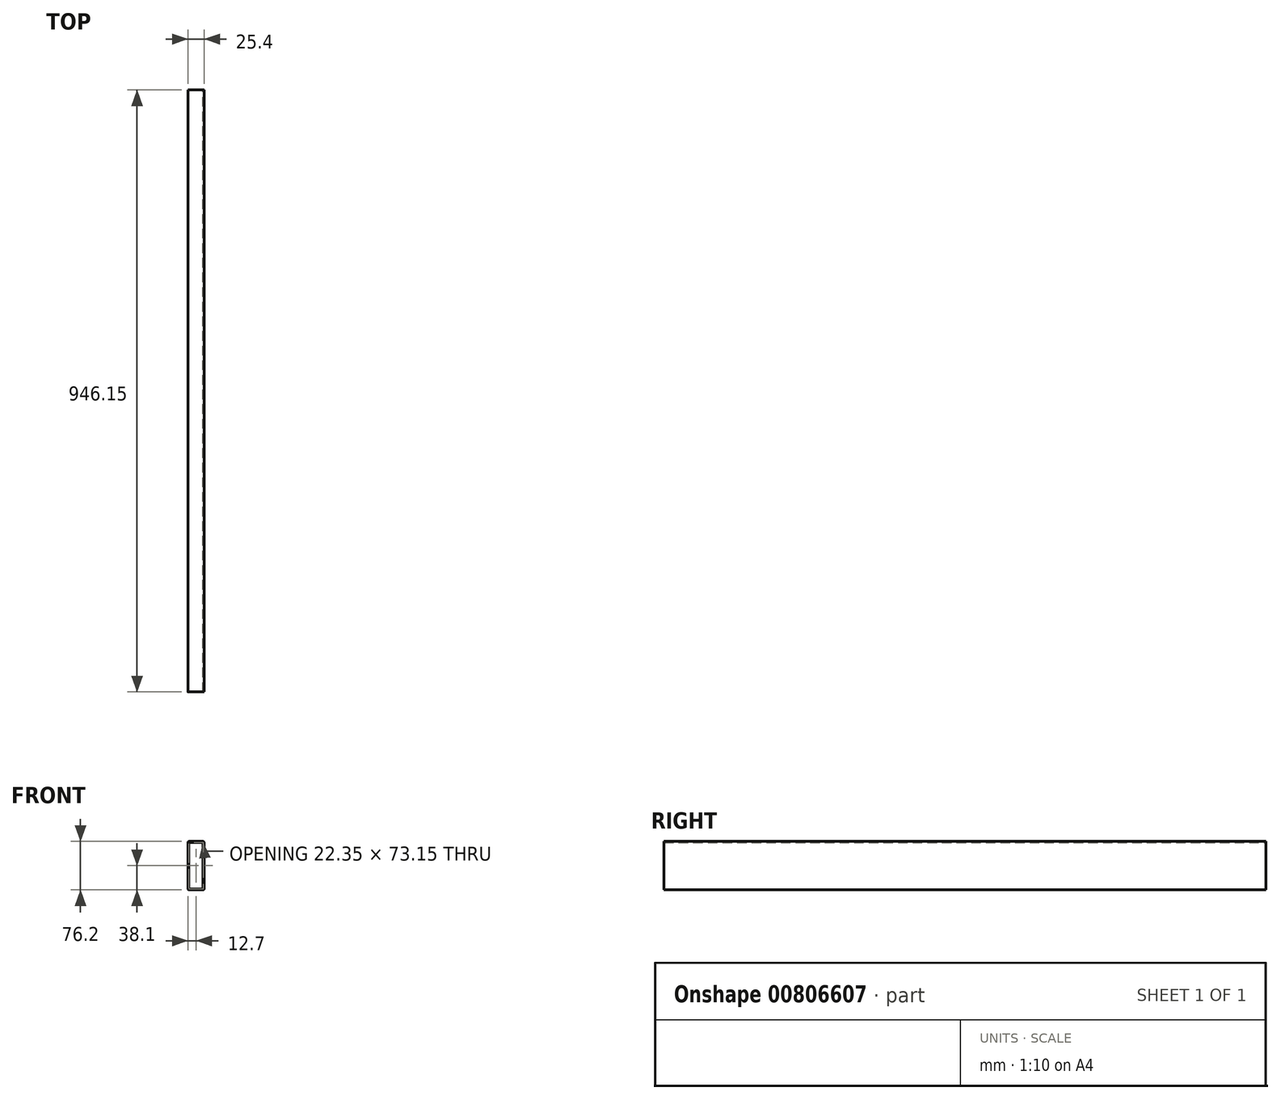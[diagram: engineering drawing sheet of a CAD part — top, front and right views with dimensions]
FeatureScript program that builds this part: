
annotation { "Feature Type Name" : "Feature", "Feature Type Description" : "" }
export const myFeature = defineFeature(function(context is Context, id is Id, definition is map)
    precondition{}
    {
        {
            var Q0;
            Q0=qCreatedBy(makeId("Front.planeOp"),FACE);
            var sketch = newSketch(context, id + "F0", { "sketchPlane" : qUnion([Q0])});
            skLineSegment(sketch, "E0.bottom", {"start": v(1.65, 0) * mm, "end": v(23.75, 0) * mm});
            skLineSegment(sketch, "E0.top", {"start": v(1.65, 76.2) * mm, "end": v(23.75, 76.2) * mm});
            skLineSegment(sketch, "E0.left", {"start": v(0, 1.65) * mm, "end": v(0, 74.55) * mm});
            skLineSegment(sketch, "E0.right", {"start": v(25.4, 1.65) * mm, "end": v(25.4, 74.55) * mm});
            skPoint(sketch, "E1.visualSharp", {"position": v(0, 76.2) * mm});
            skArc(sketch, "E1.filletArc", {"start": v(1.65, 76.2) * mm, "mid": v(0.48, 75.72) * mm, "end": v(0, 74.55) * mm});
            skPoint(sketch, "E2.visualSharp", {"position": v(25.4, 76.2) * mm});
            skArc(sketch, "E2.filletArc", {"start": v(25.4, 74.55) * mm, "mid": v(24.92, 75.72) * mm, "end": v(23.75, 76.2) * mm});
            skPoint(sketch, "E3.visualSharp", {"position": v(25.4, 0) * mm});
            skArc(sketch, "E3.filletArc", {"start": v(23.75, 0) * mm, "mid": v(24.92, 0.48) * mm, "end": v(25.4, 1.65) * mm});
            skPoint(sketch, "E4.visualSharp", {"position": v(0, 0) * mm});
            skArc(sketch, "E4.filletArc", {"start": v(0, 1.65) * mm, "mid": v(0.48, 0.48) * mm, "end": v(1.65, 0) * mm});
            skArc(sketch, "E5.0", {"start": v(1.65, 74.68) * mm, "mid": v(1.56, 74.64) * mm, "end": v(1.52, 74.55) * mm});
            skLineSegment(sketch, "E5.1", {"start": v(1.52, 1.65) * mm, "end": v(1.52, 74.55) * mm});
            skLineSegment(sketch, "E5.2", {"start": v(1.65, 74.68) * mm, "end": v(23.75, 74.68) * mm});
            skArc(sketch, "E5.3", {"start": v(1.52, 1.65) * mm, "mid": v(1.56, 1.56) * mm, "end": v(1.65, 1.52) * mm});
            skArc(sketch, "E5.4", {"start": v(23.88, 74.55) * mm, "mid": v(23.84, 74.64) * mm, "end": v(23.75, 74.68) * mm});
            skLineSegment(sketch, "E5.5", {"start": v(23.88, 1.65) * mm, "end": v(23.88, 74.55) * mm});
            skArc(sketch, "E5.6", {"start": v(23.75, 1.52) * mm, "mid": v(23.84, 1.56) * mm, "end": v(23.88, 1.65) * mm});
            skLineSegment(sketch, "E5.7", {"start": v(1.65, 1.52) * mm, "end": v(23.75, 1.52) * mm});
            skSolve(sketch);
        }
        {
            var Q0;
            Q0=makeQuery(id+"F0.imprint","IMPRINT",FACE,{"disambiguationData":[TD([[makeQuery(id+"F0.imprint","IMPRINT",EDGE,{"derivedFrom":sQuery(id+"F0.wireOp",EDGE,"fa1c825e-8885-4668-86f4-460539bfde8e.0")}),1.0]])]});
            var Q1;
            Q1=makeQuery(id+"F0.imprint","IMPRINT",FACE,{"disambiguationData":[TD([[makeQuery(id+"F0.imprint","IMPRINT",EDGE,{"derivedFrom":sQuery(id+"F0.wireOp",EDGE,"E0.bottom")}),1.0]])]});
            extrude(context, id + "F1", {"entities" : qUnion([Q0, Q1]), "depth" : 946.15 * mm, "offsetDistance" : 25.4 * mm});
        }
    });
